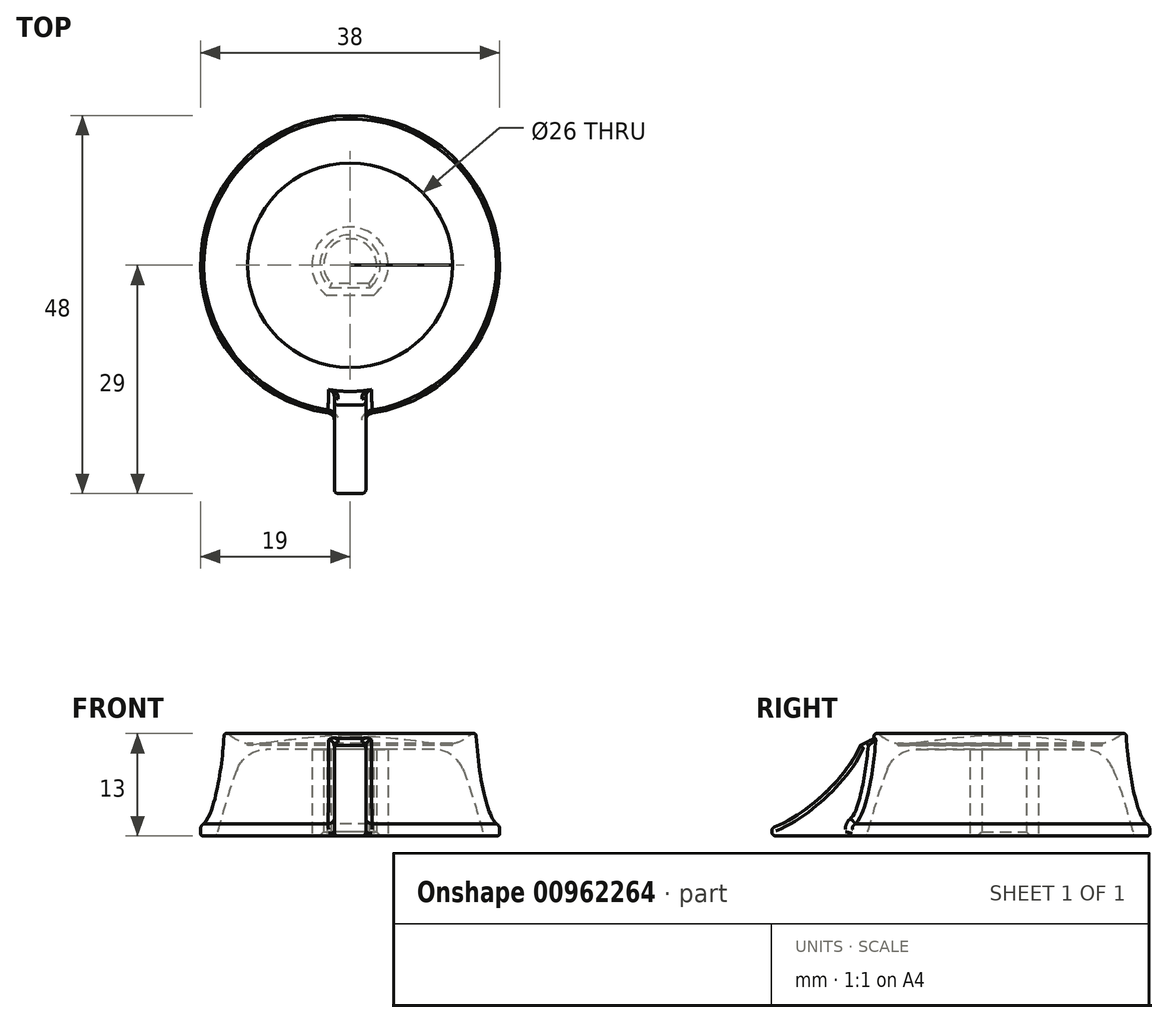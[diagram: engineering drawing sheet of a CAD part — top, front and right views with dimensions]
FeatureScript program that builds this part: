
annotation { "Feature Type Name" : "Feature", "Feature Type Description" : "" }
export const myFeature = defineFeature(function(context is Context, id is Id, definition is map)
    precondition{}
    {
        {
            var Q0;
            Q0=qCreatedBy(makeId("Top.planeOp"),FACE);
            var sketch = newSketch(context, id + "F0", { "sketchPlane" : qUnion([Q0])});
            skCircle(sketch, "E0", {"center": v(0, 0) * mm, "radius": 3.35 * mm});
            skCircle(sketch, "E1.0", {"center": v(0, 0) * mm, "radius": 4.85 * mm});
            skLineSegment(sketch, "E2", {"start": v(0, 3.35) * mm, "end": v(0, -2.35) * mm});
            skLineSegment(sketch, "E3", {"start": v(0, -2.35) * mm, "end": v(-2.39, -2.35) * mm});
            skLineSegment(sketch, "E4", {"start": v(0, -2.35) * mm, "end": v(2.39, -2.35) * mm});
            skLineSegment(sketch, "E5", {"start": v(0, -2.35) * mm, "end": v(0, -3.85) * mm});
            skLineSegment(sketch, "E6", {"start": v(0, -3.85) * mm, "end": v(2.95, -3.85) * mm});
            skLineSegment(sketch, "E7.MirrorCS", {"start": v(0, -3.85) * mm, "end": v(-2.95, -3.85) * mm});
            skSolve(sketch);
        }
        {
            var Q0;
            {var subQ0=sQuery(id+"F0.wireOp",EDGE,"7947e357-6f05-4dee-a542-af6e2948d2c70.MirrorCS");Q0=makeQuery(id+"F0.imprint","IMPRINT",FACE,{"disambiguationData":[TD([[makeQuery(id+"F0.imprint","IMPRINT",EDGE,{"derivedFrom":subQ0}),-1.0]])]});}
            var Q1;
            {var subQ0=sQuery(id+"F0.wireOp",EDGE,"Y5WQOuMT-cVHu-4DSh-Ce40-maHYm8S4J697");Q1=makeQuery(id+"F0.imprint","IMPRINT",FACE,{"disambiguationData":[TD([[makeQuery(id+"F0.imprint","IMPRINT",EDGE,{"derivedFrom":subQ0}),1.0]])]});}
            var Q2;
            Q2=makeQuery(id+"F0.imprint","IMPRINT",FACE,{"disambiguationData":[TD([[makeQuery(id+"F0.imprint","IMPRINT",EDGE,{"derivedFrom":sQuery(id+"F0.wireOp",EDGE,"8eeeedb4-f3df-42f5-852e-57c4ee479f4b.0")}),1.0]])]});
            var Q3;
            Q3=makeQuery(id+"F0.imprint","IMPRINT",FACE,{"disambiguationData":[TD([[makeQuery(id+"F0.imprint","IMPRINT",EDGE,{"derivedFrom":sQuery(id+"F0.wireOp",EDGE,"44e16a63-7607-4f80-ba96-4a3cafff2ea6.0")}),1.0]])]});
            var Q4;
            {var subQ0=sQuery(id+"F0.wireOp",EDGE,"E3");Q4=makeQuery(id+"F0.imprint","IMPRINT",FACE,{"disambiguationData":[TD([[makeQuery(id+"F0.imprint","IMPRINT",EDGE,{"derivedFrom":subQ0}),1.0]])]});}
            var Q5;
            {var subQ0=sQuery(id+"F0.wireOp",EDGE,"E4");Q5=makeQuery(id+"F0.imprint","IMPRINT",FACE,{"disambiguationData":[TD([[makeQuery(id+"F0.imprint","IMPRINT",EDGE,{"derivedFrom":subQ0}),-1.0]])]});}
            var Q6;
            {var subQ6=sQuery(id+"F0.wireOp",EDGE,"E6");Q6=makeQuery(id+"F0.imprint","IMPRINT",FACE,{"disambiguationData":[TD([[makeQuery(id+"F0.imprint","IMPRINT",EDGE,{"derivedFrom":subQ6}),1.0]])]});}
            extrude(context, id + "F1", {"entities" : qUnion([Q0, Q1, Q2, Q3, Q4, Q5, Q6]), "depth" : 11 * mm, "offsetDistance" : 25 * mm});
        }
        {
            var Q0;
            Q0=makeQuery(id+"F1.opExtrude","CAP_FACE",FACE,{"disambiguationData":[OSD([sQuery(id+"F0.wireOp",EDGE,"E0"),sQuery(id+"F0.wireOp",EDGE,"Y5WQOuMT-cVHu-4DSh-Ce40-maHYm8S4J697"),sQuery(id+"F0.wireOp",EDGE,"kEJ5qN81-GEAy-weCY-tkGc-xvZrv5ukLMXi"),sQuery(id+"F0.wireOp",EDGE,"7947e357-6f05-4dee-a542-af6e2948d2c70.MirrorCS"),sQuery(id+"F0.wireOp",EDGE,"c2cf8ceb-76f0-49b6-86e0-33dab8e645c80.MirrorCS"),sQuery(id+"F0.wireOp",EDGE,"E1.0")])],"isStart":false});
            cPlane(context, id + "F2", {"entities" : qUnion([Q0]), "cplaneType" : CPlaneType.OFFSET, "offset" : 0 * mm, "width" : 150 * mm, "height" : 150 * mm});
        }
        {
            var Q0;
            Q0=qCreatedBy(id+"F2.planeOp",FACE);
            var sketch = newSketch(context, id + "F3", { "sketchPlane" : qUnion([Q0])});
            skCircle(sketch, "E8", {"center": v(0, 0) * mm, "radius": 5.9 * mm});
            skCircle(sketch, "E9.0", {"center": v(0, 0) * mm, "radius": 13 * mm});
            skSolve(sketch);
        }
        {
            var Q0;
            Q0=qSketchRegion(id+"F3",true);
            var Q1;
            Q1=makeQuery(id+"F3.imprint","IMPRINT",FACE,{"disambiguationData":[TD([[makeQuery(id+"F3.imprint","IMPRINT",EDGE,{"derivedFrom":sQuery(id+"F3.wireOp",EDGE,"E8")}),1.0]])]});
            extrude(context, id + "F4", {"entities" : qUnion([Q0, Q1]), "operationType" : NewBodyOperationType.ADD, "depth" : .5 * mm, "offsetDistance" : 25 * mm});
        }
        {
            var Q0;
            Q0=qCreatedBy(makeId("Front.planeOp"),FACE);
            var sketch = newSketch(context, id + "F5", { "sketchPlane" : qUnion([Q0])});
            skLineSegment(sketch, "E10", {"start": v(0, 0) * mm, "end": v(0, 12.75) * mm});
            skLineSegment(sketch, "E11", {"start": v(0, 12.75) * mm, "end": v(13, 12.75) * mm});
            skLineSegment(sketch, "E12", {"start": v(13, 12.75) * mm, "end": v(13, 11.5) * mm});
            skFitSpline(sketch, "E13", {"points": [v(0, 12.75) * mm, v(13, 11.5) * mm], "startDerivative": vector(14.33, -0.14) * mm, "endDerivative": vector(7.51, -0.84) * mm});
            skLineSegment(sketch, "E14", {"start": v(13, 10.78) * mm, "end": v(13, 12.75) * mm});
            skLineSegment(sketch, "E15.top", {"start": v(0, 10.78) * mm, "end": v(13, 10.78) * mm});
            skLineSegment(sketch, "E15.left", {"start": v(0, 10.78) * mm, "end": v(0, 12.75) * mm});
            skLineSegment(sketch, "E16", {"start": v(13, 11.25) * mm, "end": v(0, 11.25) * mm});
            skSolve(sketch);
        }
        {
            var Q0;
            {var subQ0=sQuery(id+"F5.wireOp",EDGE,"E13");Q0=makeQuery(id+"F5.imprint","IMPRINT",FACE,{"disambiguationData":[TD([[makeQuery(id+"F5.imprint","IMPRINT",EDGE,{"derivedFrom":subQ0}),-1.0]])]});}
            var Q1;
            Q1=makeQuery(id+"F4.opExtrude","SWEPT_FACE",FACE,{"disambiguationData":[OSD([sQuery(id+"F3.wireOp",EDGE,"E9.0")])]});
            revolve(context, id + "F6", {"operationType" : NewBodyOperationType.ADD, "surfaceOperationType" : NewSurfaceOperationType.NEW, "entities" : qUnion([Q0]), "axis" : qUnion([Q1]), "revolveType" : RevolveType.FULL, "oppositeDirection" : true});
        }
        {
            var Q0;
            Q0=qCreatedBy(makeId("Front.planeOp"),FACE);
            var sketch = newSketch(context, id + "F7", { "sketchPlane" : qUnion([Q0])});
            skLineSegment(sketch, "E17", {"start": v(0, 0) * mm, "end": v(19, 0) * mm});
            skLineSegment(sketch, "E18", {"start": v(19, 0) * mm, "end": v(19, 0.8) * mm});
            skLineSegment(sketch, "E19", {"start": v(19, 0.8) * mm, "end": v(19, 9.8) * mm});
            skLineSegment(sketch, "E20", {"start": v(0, 0) * mm, "end": v(0, 11) * mm});
            skLineSegment(sketch, "E21", {"start": v(0, 11) * mm, "end": v(13, 11) * mm});
            skLineSegment(sketch, "E22", {"start": v(13, 11) * mm, "end": v(13, 13) * mm});
            skLineSegment(sketch, "E23", {"start": v(13, 13) * mm, "end": v(15.5, 13) * mm});
            skLineSegment(sketch, "E24", {"start": v(15.5, 13) * mm, "end": v(16, 13) * mm});
            skLineSegment(sketch, "E25", {"start": v(19, 0.8) * mm, "end": v(18.6, 0.8) * mm});
            skLineSegment(sketch, "E26", {"start": v(18.6, 0.8) * mm, "end": v(18.6, 1.55) * mm});
            skFitSpline(sketch, "E27", {"points": [v(16, 13) * mm, v(18.6, 1.55) * mm], "startDerivative": vector(0.75, -14.7) * mm, "endDerivative": vector(3.82, -3.03) * mm});
            skFitSpline(sketch, "E28", {"points": [v(18.6, 1.55) * mm, v(19, 0.8) * mm], "startDerivative": vector(0.5, -0.48) * mm, "endDerivative": vector(0, -1.47) * mm});
            skLineSegment(sketch, "E29", {"start": v(13, 11) * mm, "end": v(13, 11.75) * mm});
            skLineSegment(sketch, "E30", {"start": v(13, 11.75) * mm, "end": v(13, 11.75) * mm});
            skFitSpline(sketch, "E31", {"points": [v(13, 11.75) * mm, v(15.5, 13) * mm], "startDerivative": vector(3.02, 0.3) * mm, "endDerivative": vector(1.5, 1.36) * mm});
            skLineSegment(sketch, "E32", {"start": v(19, 0) * mm, "end": v(17, 0) * mm});
            skFitSpline(sketch, "E33", {"points": [v(13, 11) * mm, v(17, 0) * mm], "startDerivative": vector(5.15, -6.81) * mm, "endDerivative": vector(2.57, -8.62) * mm});
            skLineSegment(sketch, "E34", {"start": v(19, 0) * mm, "end": v(23.98, 0) * mm});
            skLineSegment(sketch, "E35", {"start": v(23.98, 0) * mm, "end": v(23.98, 13) * mm});
            skSolve(sketch);
        }
        {
            var Q0;
            Q0=makeQuery(id+"F7.imprint","IMPRINT",FACE,{"disambiguationData":[TD([[makeQuery(id+"F7.imprint","IMPRINT",EDGE,{"derivedFrom":sQuery(id+"F7.wireOp",EDGE,"E25")}),-1.0]])]});
            var Q1;
            Q1=makeQuery(id+"F7.imprint","IMPRINT",FACE,{"disambiguationData":[TD([[makeQuery(id+"F7.imprint","IMPRINT",EDGE,{"derivedFrom":sQuery(id+"F7.wireOp",EDGE,"E18")}),1.0]])]});
            var Q2;
            Q2=makeQuery(id+"F4.opExtrude","SWEPT_FACE",FACE,{"disambiguationData":[OSD([sQuery(id+"F3.wireOp",EDGE,"E9.0")])]});
            revolve(context, id + "F8", {"operationType" : NewBodyOperationType.ADD, "surfaceOperationType" : NewSurfaceOperationType.NEW, "entities" : qUnion([Q0, Q1]), "axis" : qUnion([Q2]), "revolveType" : RevolveType.FULL});
        }
        {
            var Q0;
            Q0=makeQuery(id+"F8.opRevolve","SWEPT_EDGE",EDGE,{"disambiguationData":[OSD([sQuery(id+"F7.wireOp",EDGE,"E24"),sQuery(id+"F7.wireOp",EDGE,"E27")])]});
            var Q1;
            Q1=makeQuery(id+"F8.opRevolve","SWEPT_EDGE",EDGE,{"disambiguationData":[OSD([sQuery(id+"F7.wireOp",EDGE,"E23"),sQuery(id+"F7.wireOp",EDGE,"E24"),sQuery(id+"F7.wireOp",EDGE,"E31")])]});
            var Q2;
            Q2=makeQuery(id+"F8.opRevolve","SWEPT_EDGE",EDGE,{"disambiguationData":[OSD([sQuery(id+"F7.wireOp",EDGE,"E18"),sQuery(id+"F7.wireOp",EDGE,"E32")])]});
            var Q3;
            Q3=makeQuery(id+"F8.opRevolve","SWEPT_EDGE",EDGE,{"disambiguationData":[OSD([sQuery(id+"F7.wireOp",EDGE,"E17"),sQuery(id+"F7.wireOp",EDGE,"E32"),sQuery(id+"F7.wireOp",EDGE,"E33")])]});
            fillet(context, id + "F9", {"entities" : qUnion([Q0, Q1, Q2, Q3]), "radius" : .3 * mm, "tangentPropagation" : true, "allowEdgeOverflow" : false});
        }
        {
            var Q0;
            Q0=makeQuery(id+"F1.opExtrude","CAP_EDGE",EDGE,{"disambiguationData":[OSD([sQuery(id+"F0.wireOp",EDGE,"E1.0")])],"isStart":false});
            var Q1;
            Q1=makeQuery(id+"F1.opExtrude","CAP_EDGE",EDGE,{"disambiguationData":[OSD([sQuery(id+"F0.wireOp",EDGE,"E6"),sQuery(id+"F0.wireOp",EDGE,"E7.MirrorCS")])],"isStart":false});
            var Q2;
            Q2=makeQuery(id+"F8.boolean.opBoolean","MERGE",EDGE,{"derivedFrom":[makeQuery(id+"F4.opExtrude","CAP_EDGE",EDGE,{"disambiguationData":[OSD([sQuery(id+"F3.wireOp",EDGE,"E9.0")])],"isStart":true}),makeQuery(id+"F8.opRevolve","SWEPT_EDGE",EDGE,{"disambiguationData":[OSD([sQuery(id+"F7.wireOp",EDGE,"E21"),sQuery(id+"F7.wireOp",EDGE,"E29"),sQuery(id+"F7.wireOp",EDGE,"E33")])]})]});
            fillet(context, id + "F10", {"entities" : qUnion([Q0, Q1, Q2]), "radius" : 4 * mm, "tangentPropagation" : true, "allowEdgeOverflow" : false});
        }
        {
            var Q0;
            Q0=makeQuery(id+"F1.opExtrude","CAP_EDGE",EDGE,{"disambiguationData":[OSD([sQuery(id+"F0.wireOp",EDGE,"c2cf8ceb-76f0-49b6-86e0-33dab8e645c80.MirrorCS")])],"isStart":true});
            var Q1;
            Q1=makeQuery(id+"F1.opExtrude","CAP_EDGE",EDGE,{"disambiguationData":[OSD([sQuery(id+"F0.wireOp",EDGE,"7947e357-6f05-4dee-a542-af6e2948d2c70.MirrorCS")])],"isStart":true});
            var Q2;
            Q2=makeQuery(id+"F1.opExtrude","CAP_EDGE",EDGE,{"disambiguationData":[OSD([sQuery(id+"F0.wireOp",EDGE,"kEJ5qN81-GEAy-weCY-tkGc-xvZrv5ukLMXi")])],"isStart":true});
            var Q3;
            Q3=makeQuery(id+"F1.opExtrude","CAP_EDGE",EDGE,{"disambiguationData":[OSD([sQuery(id+"F0.wireOp",EDGE,"Y5WQOuMT-cVHu-4DSh-Ce40-maHYm8S4J697")])],"isStart":true});
            var Q4;
            {var subQ0=sQuery(id+"F0.wireOp",EDGE,"E0");var subQ1=makeQuery(id+"F0.imprint","INTERSECT",VERTEX,{"derivedFrom":[subQ0,sQuery(id+"F0.wireOp",EDGE,"NaaVB31x-4mlA-R9wx-hKtx-BvIfxYHzTa7V")]});Q4=makeQuery(id+"F1.opExtrude","CAP_EDGE",EDGE,{"disambiguationData":[OSD([subQ0]),TDD([makeQuery(id+"F0.imprint","IMPRINT",EDGE,{"disambiguationData":[TD([[subQ1,1.0]])],"derivedFrom":subQ0}),makeQuery(id+"F0.imprint","IMPRINT",EDGE,{"disambiguationData":[TD([[subQ1,-1.0]])],"derivedFrom":subQ0})])],"isStart":true});}
            var Q5;
            {var subQ0=sQuery(id+"F0.wireOp",EDGE,"E0");Q5=makeQuery(id+"F1.opExtrude","CAP_EDGE",EDGE,{"disambiguationData":[OSD([subQ0]),TDD([makeQuery(id+"F0.imprint","IMPRINT",EDGE,{"disambiguationData":[TD([[makeQuery(id+"F0.imprint","INTERSECT",VERTEX,{"derivedFrom":[subQ0,sQuery(id+"F0.wireOp",EDGE,"Y5WQOuMT-cVHu-4DSh-Ce40-maHYm8S4J697")]}),-1.0]])],"derivedFrom":subQ0})])],"isStart":true});}
            var Q6;
            Q6=makeQuery(id+"F5ZplvMa2vL8Z5Y_1.boolean.opBoolean","COPY",EDGE,{"derivedFrom":makeQuery(id+"F5ZplvMa2vL8Z5Y_1.opExtrude","CAP_EDGE",EDGE,{"disambiguationData":[OSD([sQuery(id+"F0.wireOp",EDGE,"44e16a63-7607-4f80-ba96-4a3cafff2ea6.0")])],"isStart":true})});
            var Q7;
            Q7=makeQuery(id+"F5ZplvMa2vL8Z5Y_1.boolean.opBoolean","COPY",EDGE,{"derivedFrom":makeQuery(id+"F5ZplvMa2vL8Z5Y_1.opExtrude","CAP_EDGE",EDGE,{"disambiguationData":[OSD([sQuery(id+"F0.wireOp",EDGE,"8eeeedb4-f3df-42f5-852e-57c4ee479f4b.0")])],"isStart":true})});
            var Q8;
            Q8=makeQuery(id+"F1.opExtrude","CAP_EDGE",EDGE,{"disambiguationData":[OSD([sQuery(id+"F0.wireOp",EDGE,"E3"),sQuery(id+"F0.wireOp",EDGE,"E4")])],"isStart":true});
            chamfer(context, id + "F11", {"entities" : qUnion([Q0, Q1, Q2, Q3, Q4, Q5, Q6, Q7, Q8]), "width" : .5 * mm, "tangentPropagation" : true});
        }
        {
            var Q0;
            Q0=qCreatedBy(makeId("Right.planeOp"),FACE);
            var sketch = newSketch(context, id + "F12", { "sketchPlane" : qUnion([Q0])});
            skLineSegment(sketch, "E36", {"start": v(0, 0) * mm, "end": v(-18, 0) * mm});
            skLineSegment(sketch, "E37", {"start": v(-18, 0) * mm, "end": v(-18, 1.36) * mm});
            skLineSegment(sketch, "E38", {"start": v(-18, 1.36) * mm, "end": v(-16.85, 4.45) * mm});
            skLineSegment(sketch, "E39", {"start": v(-16.85, 4.45) * mm, "end": v(-16, 8.95) * mm});
            skLineSegment(sketch, "E40", {"start": v(-16, 8.95) * mm, "end": v(-15.79, 12.5) * mm});
            skLineSegment(sketch, "E41", {"start": v(-15.79, 12.5) * mm, "end": v(-17.76, 11.51) * mm});
            skLineSegment(sketch, "E42", {"start": v(-18, 0) * mm, "end": v(-29, 0) * mm});
            skLineSegment(sketch, "E43", {"start": v(-29, 0) * mm, "end": v(-29, 1) * mm});
            skFitSpline(sketch, "E44", {"points": [v(-17.76, 11.51) * mm, v(-29, 1) * mm], "startDerivative": vector(-5.04, -12.25) * mm, "endDerivative": vector(-12.59, -4.46) * mm});
            skSolve(sketch);
        }
        {
            var Q0;
            Q0 = qSketchRegion(id + "F12", true);
            extrude(context, id + "F13", {"entities" : qUnion([Q0]), "operationType" : NewBodyOperationType.ADD, "depth" : 2 * mm, "offsetDistance" : 25 * mm, "hasSecondDirection" : true, "secondDirectionOppositeDirection" : true, "secondDirectionDepth" : 2 * mm});
        }
        {
            var Q0;
            Q0=makeQuery(id+"F13.boolean.opBoolean","INTERSECT",EDGE,{"derivedFrom":[makeQuery(id+"F8.opRevolve","SWEPT_FACE",FACE,{"disambiguationData":[OSD([sQuery(id+"F7.wireOp",EDGE,"E27")])]}),makeQuery(id+"F13.opExtrude","CAP_FACE",FACE,{"disambiguationData":[OSD([sQuery(id+"F12.wireOp",EDGE,"E37"),sQuery(id+"F12.wireOp",EDGE,"E38"),sQuery(id+"F12.wireOp",EDGE,"E39"),sQuery(id+"F12.wireOp",EDGE,"E40"),sQuery(id+"F12.wireOp",EDGE,"E41"),sQuery(id+"F12.wireOp",EDGE,"E42"),sQuery(id+"F12.wireOp",EDGE,"E43"),sQuery(id+"F12.wireOp",EDGE,"E44")])],"isStart":true})]});
            var Q1;
            Q1=makeQuery(id+"F13.boolean.opBoolean","INTERSECT",EDGE,{"derivedFrom":[makeQuery(id+"F8.opRevolve","SWEPT_FACE",FACE,{"disambiguationData":[OSD([sQuery(id+"F7.wireOp",EDGE,"E28")])]}),makeQuery(id+"F13.opExtrude","CAP_FACE",FACE,{"disambiguationData":[OSD([sQuery(id+"F12.wireOp",EDGE,"E37"),sQuery(id+"F12.wireOp",EDGE,"E38"),sQuery(id+"F12.wireOp",EDGE,"E39"),sQuery(id+"F12.wireOp",EDGE,"E40"),sQuery(id+"F12.wireOp",EDGE,"E41"),sQuery(id+"F12.wireOp",EDGE,"E42"),sQuery(id+"F12.wireOp",EDGE,"E43"),sQuery(id+"F12.wireOp",EDGE,"E44")])],"isStart":true})]});
            var Q2;
            Q2=makeQuery(id+"F13.boolean.opBoolean","INTERSECT",EDGE,{"derivedFrom":[makeQuery(id+"F8.opRevolve","SWEPT_FACE",FACE,{"disambiguationData":[OSD([sQuery(id+"F7.wireOp",EDGE,"E18")])]}),makeQuery(id+"F13.opExtrude","CAP_FACE",FACE,{"disambiguationData":[OSD([sQuery(id+"F12.wireOp",EDGE,"E37"),sQuery(id+"F12.wireOp",EDGE,"E38"),sQuery(id+"F12.wireOp",EDGE,"E39"),sQuery(id+"F12.wireOp",EDGE,"E40"),sQuery(id+"F12.wireOp",EDGE,"E41"),sQuery(id+"F12.wireOp",EDGE,"E42"),sQuery(id+"F12.wireOp",EDGE,"E43"),sQuery(id+"F12.wireOp",EDGE,"E44")])],"isStart":true})]});
            var Q3;
            Q3=makeQuery(id+"F13.boolean.opBoolean","INTERSECT",EDGE,{"derivedFrom":[makeQuery(id+"F9.opFillet","BLEND_FACE",FACE,{"disambiguationData":[OSD([sQuery(id+"F7.wireOp",EDGE,"E18"),sQuery(id+"F7.wireOp",EDGE,"E32")])]}),makeQuery(id+"F13.opExtrude","CAP_FACE",FACE,{"disambiguationData":[OSD([sQuery(id+"F12.wireOp",EDGE,"E37"),sQuery(id+"F12.wireOp",EDGE,"E38"),sQuery(id+"F12.wireOp",EDGE,"E39"),sQuery(id+"F12.wireOp",EDGE,"E40"),sQuery(id+"F12.wireOp",EDGE,"E41"),sQuery(id+"F12.wireOp",EDGE,"E42"),sQuery(id+"F12.wireOp",EDGE,"E43"),sQuery(id+"F12.wireOp",EDGE,"E44")])],"isStart":true})]});
            var Q4;
            Q4=makeQuery(id+"F13.boolean.opBoolean","INTERSECT",EDGE,{"derivedFrom":[makeQuery(id+"F8.opRevolve","SWEPT_FACE",FACE,{"disambiguationData":[OSD([sQuery(id+"F7.wireOp",EDGE,"E27")])]}),makeQuery(id+"F13.opExtrude","CAP_FACE",FACE,{"disambiguationData":[OSD([sQuery(id+"F12.wireOp",EDGE,"E37"),sQuery(id+"F12.wireOp",EDGE,"E38"),sQuery(id+"F12.wireOp",EDGE,"E39"),sQuery(id+"F12.wireOp",EDGE,"E40"),sQuery(id+"F12.wireOp",EDGE,"E41"),sQuery(id+"F12.wireOp",EDGE,"E42"),sQuery(id+"F12.wireOp",EDGE,"E43"),sQuery(id+"F12.wireOp",EDGE,"E44")])],"isStart":false})]});
            var Q5;
            Q5=makeQuery(id+"F13.boolean.opBoolean","INTERSECT",EDGE,{"derivedFrom":[makeQuery(id+"F8.opRevolve","SWEPT_FACE",FACE,{"disambiguationData":[OSD([sQuery(id+"F7.wireOp",EDGE,"E28")])]}),makeQuery(id+"F13.opExtrude","CAP_FACE",FACE,{"disambiguationData":[OSD([sQuery(id+"F12.wireOp",EDGE,"E37"),sQuery(id+"F12.wireOp",EDGE,"E38"),sQuery(id+"F12.wireOp",EDGE,"E39"),sQuery(id+"F12.wireOp",EDGE,"E40"),sQuery(id+"F12.wireOp",EDGE,"E41"),sQuery(id+"F12.wireOp",EDGE,"E42"),sQuery(id+"F12.wireOp",EDGE,"E43"),sQuery(id+"F12.wireOp",EDGE,"E44")])],"isStart":false})]});
            fillet(context, id + "F14", {"entities" : qUnion([Q0, Q1, Q2, Q3, Q4, Q5]), "radius" : .89 * mm, "tangentPropagation" : true, "allowEdgeOverflow" : false});
        }
        {
            var Q0;
            Q0=makeQuery(id+"F13.opExtrude","CAP_EDGE",EDGE,{"disambiguationData":[OSD([sQuery(id+"F12.wireOp",EDGE,"E43")])],"isStart":true});
            var Q1;
            Q1=makeQuery(id+"F13.opExtrude","CAP_EDGE",EDGE,{"disambiguationData":[OSD([sQuery(id+"F12.wireOp",EDGE,"E44")])],"isStart":true});
            var Q2;
            Q2=makeQuery(id+"F13.opExtrude","CAP_EDGE",EDGE,{"disambiguationData":[OSD([sQuery(id+"F12.wireOp",EDGE,"E41")])],"isStart":true});
            var Q3;
            Q3=makeQuery(id+"F13.opExtrude","CAP_EDGE",EDGE,{"disambiguationData":[OSD([sQuery(id+"F12.wireOp",EDGE,"E44")])],"isStart":false});
            var Q4;
            Q4=makeQuery(id+"F13.opExtrude","CAP_EDGE",EDGE,{"disambiguationData":[OSD([sQuery(id+"F12.wireOp",EDGE,"E43")])],"isStart":false});
            var Q5;
            Q5=makeQuery(id+"F13.opExtrude","CAP_EDGE",EDGE,{"disambiguationData":[OSD([sQuery(id+"F12.wireOp",EDGE,"E41")])],"isStart":false});
            var Q6;
            Q6=makeQuery(id+"F13.opExtrude","CAP_EDGE",EDGE,{"disambiguationData":[OSD([sQuery(id+"F12.wireOp",EDGE,"E42")])],"isStart":true});
            var Q7;
            Q7=makeQuery(id+"F13.opExtrude","CAP_EDGE",EDGE,{"disambiguationData":[OSD([sQuery(id+"F12.wireOp",EDGE,"E42")])],"isStart":false});
            var Q8;
            Q8=makeQuery(id+"F13.opExtrude","SWEPT_EDGE",EDGE,{"disambiguationData":[OSD([sQuery(id+"F12.wireOp",EDGE,"E43"),sQuery(id+"F12.wireOp",EDGE,"E44")])]});
            var Q9;
            Q9=makeQuery(id+"F13.opExtrude","SWEPT_EDGE",EDGE,{"disambiguationData":[OSD([sQuery(id+"F12.wireOp",EDGE,"E42"),sQuery(id+"F12.wireOp",EDGE,"E43")])]});
            fillet(context, id + "F15", {"entities" : qUnion([Q0, Q1, Q2, Q3, Q4, Q5, Q6, Q7, Q8, Q9]), "radius" : .5 * mm, "tangentPropagation" : true, "allowEdgeOverflow" : false});
        }
    });
